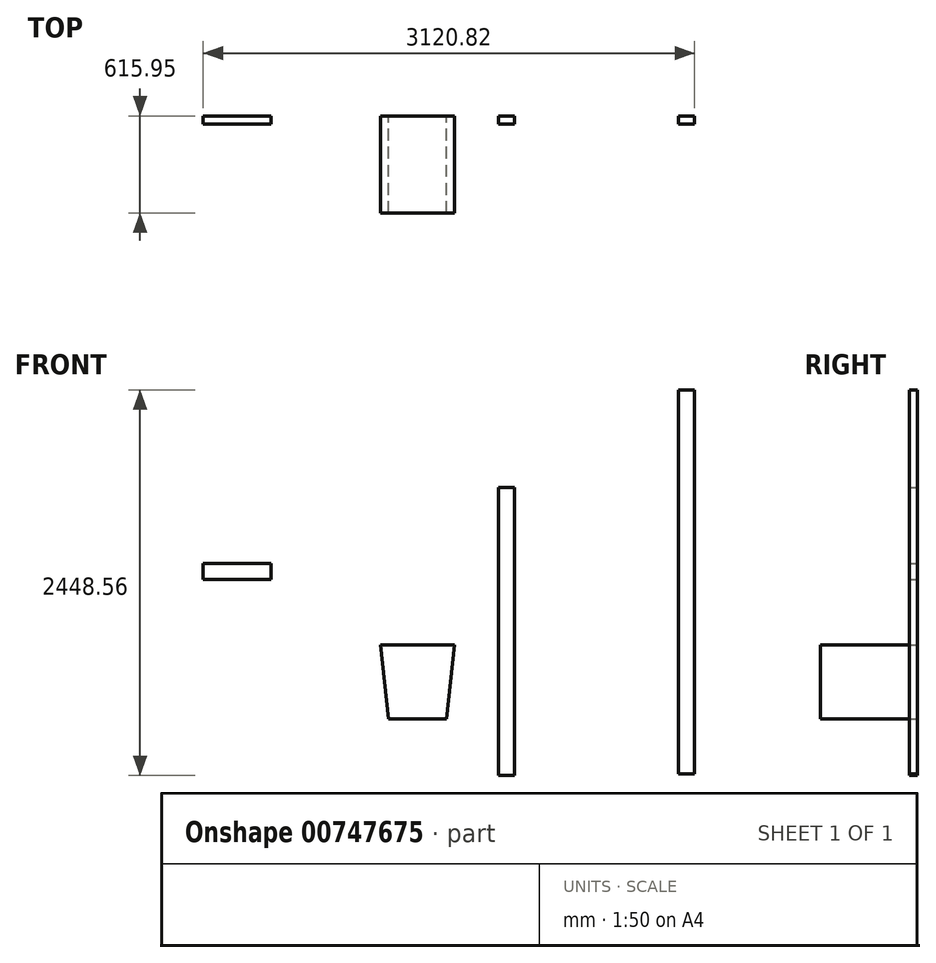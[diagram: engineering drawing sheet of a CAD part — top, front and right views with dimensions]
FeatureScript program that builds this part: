
annotation { "Feature Type Name" : "Feature", "Feature Type Description" : "" }
export const myFeature = defineFeature(function(context is Context, id is Id, definition is map)
    precondition{}
    {
        {
            var Q0;
            Q0=qCreatedBy(makeId("Front.planeOp"),FACE);
            var sketch = newSketch(context, id + "F0", { "sketchPlane" : qUnion([Q0])});
            skLineSegment(sketch, "E0.bottom", {"start": v(-763.05, 987.9) * mm, "end": v(-661.45, 987.9) * mm});
            skLineSegment(sketch, "E0.top", {"start": v(-763.05, -840.9) * mm, "end": v(-661.45, -840.9) * mm});
            skLineSegment(sketch, "E0.left", {"start": v(-763.05, 987.9) * mm, "end": v(-763.05, -840.9) * mm});
            skLineSegment(sketch, "E0.right", {"start": v(-661.45, 987.9) * mm, "end": v(-661.45, -840.9) * mm});
            skLineSegment(sketch, "E1.bottom", {"start": v(380.15, 1607.67) * mm, "end": v(481.75, 1607.67) * mm});
            skLineSegment(sketch, "E1.top", {"start": v(380.15, -830.73) * mm, "end": v(481.75, -830.73) * mm});
            skLineSegment(sketch, "E1.left", {"start": v(380.15, 1607.67) * mm, "end": v(380.15, -830.73) * mm});
            skLineSegment(sketch, "E1.right", {"start": v(481.75, 1607.67) * mm, "end": v(481.75, -830.73) * mm});
            skLineSegment(sketch, "E2", {"start": v(-1511.96, -12.62) * mm, "end": v(-1042.06, -12.62) * mm});
            skLineSegment(sketch, "E3", {"start": v(-1042.06, -12.62) * mm, "end": v(-1092.86, -479.76) * mm});
            skLineSegment(sketch, "E4", {"start": v(-1092.86, -479.76) * mm, "end": v(-1461.16, -479.76) * mm});
            skLineSegment(sketch, "E5", {"start": v(-1461.16, -479.76) * mm, "end": v(-1511.96, -12.62) * mm});
            skLineSegment(sketch, "E6.bottom", {"start": v(-2639.07, 506.74) * mm, "end": v(-2207.27, 506.74) * mm});
            skLineSegment(sketch, "E6.top", {"start": v(-2639.07, 405.14) * mm, "end": v(-2207.27, 405.14) * mm});
            skLineSegment(sketch, "E6.left", {"start": v(-2639.07, 506.74) * mm, "end": v(-2639.07, 405.14) * mm});
            skLineSegment(sketch, "E6.right", {"start": v(-2207.27, 506.74) * mm, "end": v(-2207.27, 405.14) * mm});
            skSolve(sketch);
        }
        {
            var Q0;
            Q0=makeQuery(id+"F0.imprint","IMPRINT",FACE,{"disambiguationData":[TD([[makeQuery(id+"F0.imprint","IMPRINT",EDGE,{"derivedFrom":sQuery(id+"F0.wireOp",EDGE,"E0.bottom")}),-1.0]])]});
            extrude(context, id + "F1", {"entities" : qUnion([Q0]), "depth" : 50.8 * mm, "offsetDistance" : 25.4 * mm});
        }
        {
            var Q0;
            Q0=makeQuery(id+"F0.imprint","IMPRINT",FACE,{"disambiguationData":[TD([[makeQuery(id+"F0.imprint","IMPRINT",EDGE,{"derivedFrom":sQuery(id+"F0.wireOp",EDGE,"E1.bottom")}),-1.0]])]});
            extrude(context, id + "F2", {"entities" : qUnion([Q0]), "depth" : 50.8 * mm, "offsetDistance" : 25.4 * mm});
        }
        {
            var Q0;
            Q0=makeQuery(id+"F0.imprint","IMPRINT",FACE,{"disambiguationData":[TD([[makeQuery(id+"F0.imprint","IMPRINT",EDGE,{"derivedFrom":sQuery(id+"F0.wireOp",EDGE,"E2")}),-1.0]])]});
            extrude(context, id + "F3", {"entities" : qUnion([Q0]), "depth" : 615.95 * mm, "offsetDistance" : 25.4 * mm});
        }
        {
            var Q0;
            Q0=makeQuery(id+"F0.imprint","IMPRINT",FACE,{"disambiguationData":[TD([[makeQuery(id+"F0.imprint","IMPRINT",EDGE,{"derivedFrom":sQuery(id+"F0.wireOp",EDGE,"E6.bottom")}),-1.0]])]});
            extrude(context, id + "F4", {"entities" : qUnion([Q0]), "depth" : 50.8 * mm, "offsetDistance" : 25.4 * mm});
        }
    });
